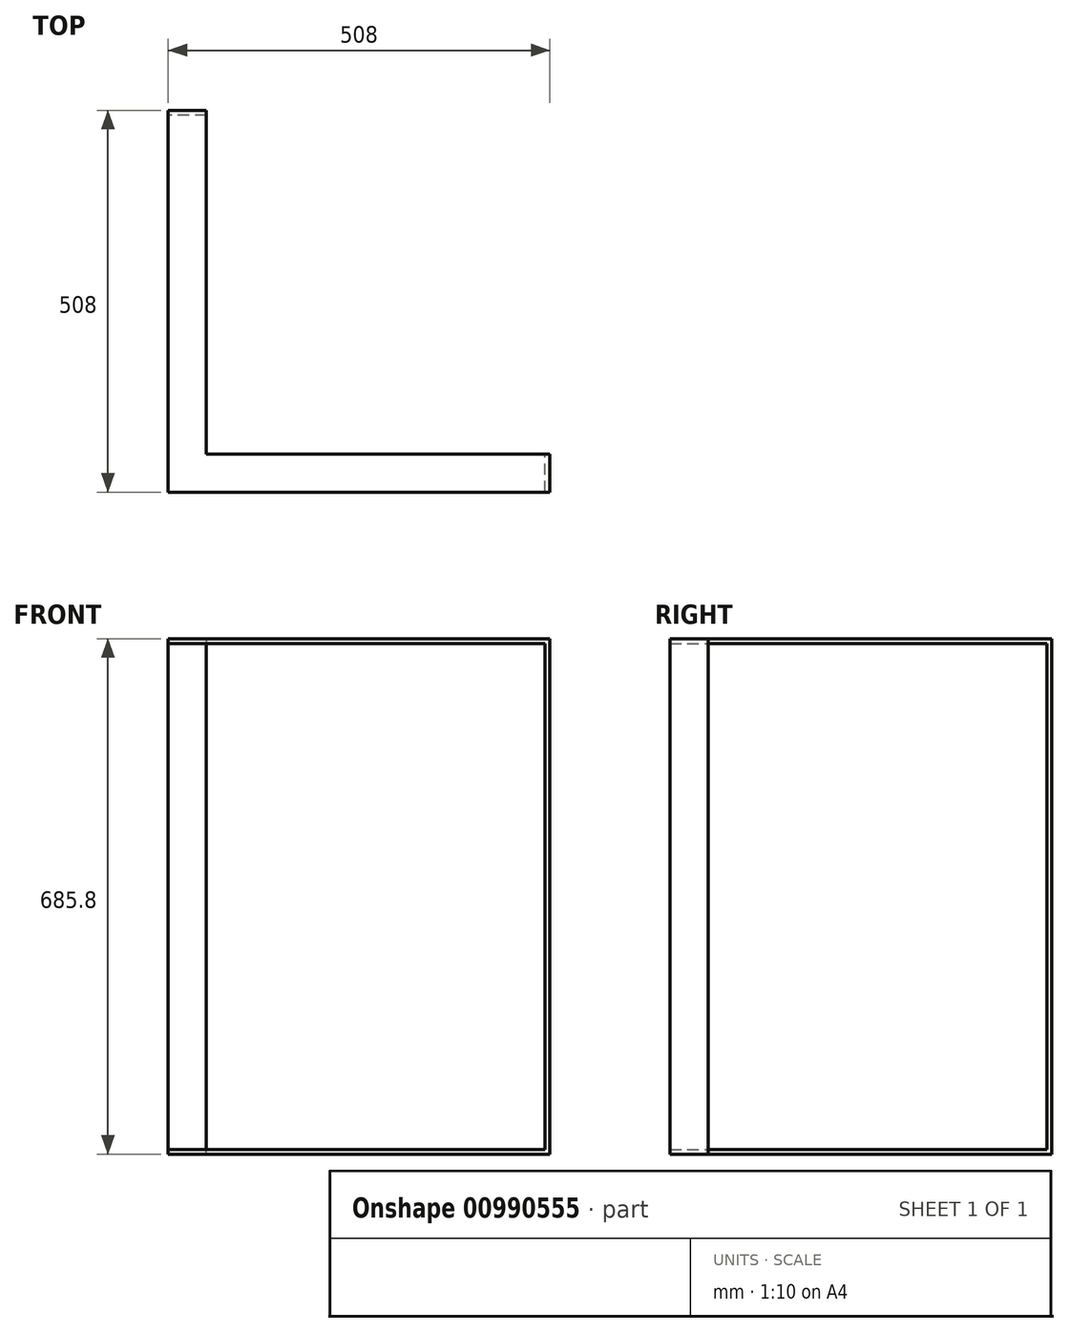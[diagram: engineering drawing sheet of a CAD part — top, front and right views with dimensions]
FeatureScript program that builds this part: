
annotation { "Feature Type Name" : "Feature", "Feature Type Description" : "" }
export const myFeature = defineFeature(function(context is Context, id is Id, definition is map)
    precondition{}
    {
        {
            var Q0;
            Q0=qCreatedBy(makeId("Top.planeOp"),FACE);
            var sketch = newSketch(context, id + "F0", { "sketchPlane" : qUnion([Q0])});
            skLineSegment(sketch, "E0", {"start": v(0, 0) * mm, "end": v(0, 457.2) * mm});
            skLineSegment(sketch, "E1", {"start": v(0, 457.2) * mm, "end": v(-50.8, 457.2) * mm});
            skLineSegment(sketch, "E2", {"start": v(-50.8, 457.2) * mm, "end": v(-50.8, -50.8) * mm});
            skLineSegment(sketch, "E3", {"start": v(-50.8, -50.8) * mm, "end": v(457.2, -50.8) * mm});
            skLineSegment(sketch, "E4", {"start": v(457.2, -50.8) * mm, "end": v(457.2, 0) * mm});
            skLineSegment(sketch, "E5", {"start": v(457.2, 0) * mm, "end": v(0, 0) * mm});
            skSolve(sketch);
        }
        {
            var Q0;
            Q0 = qSketchRegion(id + "F0", true);
            extrude(context, id + "F1", {"entities" : qUnion([Q0]), "depth" : 6.35 * mm, "offsetDistance" : 25.4 * mm});
        }
        {
            var Q0;
            Q0=makeQuery(id+"F1.opExtrude","CAP_FACE",FACE,{"disambiguationData":[OSD([sQuery(id+"F0.wireOp",EDGE,"E0"),sQuery(id+"F0.wireOp",EDGE,"E1"),sQuery(id+"F0.wireOp",EDGE,"E2"),sQuery(id+"F0.wireOp",EDGE,"E3"),sQuery(id+"F0.wireOp",EDGE,"E4"),sQuery(id+"F0.wireOp",EDGE,"E5")])],"isStart":true});
            var sketch = newSketch(context, id + "F2", { "sketchPlane" : qUnion([Q0])});
            skLineSegment(sketch, "E6.bottom", {"start": v(457.2, 50.8) * mm, "end": v(450.85, 50.8) * mm});
            skLineSegment(sketch, "E6.top", {"start": v(457.2, 0) * mm, "end": v(450.85, 0) * mm});
            skLineSegment(sketch, "E6.left", {"start": v(457.2, 50.8) * mm, "end": v(457.2, 0) * mm});
            skLineSegment(sketch, "E6.right", {"start": v(450.85, 50.8) * mm, "end": v(450.85, 0) * mm});
            skSolve(sketch);
        }
        {
            var Q0;
            Q0 = qSketchRegion(id + "F2", true);
            extrude(context, id + "F3", {"entities" : qUnion([Q0]), "operationType" : NewBodyOperationType.ADD, "depth" : 673.1 * mm, "offsetDistance" : 25.4 * mm});
        }
        {
            var Q0;
            Q0=makeQuery(id+"F3.opExtrude","CAP_FACE",FACE,{"disambiguationData":[OSD([sQuery(id+"F2.wireOp",EDGE,"E6.bottom"),sQuery(id+"F2.wireOp",EDGE,"E6.top"),sQuery(id+"F2.wireOp",EDGE,"E6.left"),sQuery(id+"F2.wireOp",EDGE,"E6.right")])],"isStart":false});
            var sketch = newSketch(context, id + "F4", { "sketchPlane" : qUnion([Q0])});
            skLineSegment(sketch, "E7", {"start": v(457.2, 50.8) * mm, "end": v(-50.8, 50.8) * mm});
            skLineSegment(sketch, "E8", {"start": v(-50.8, 50.8) * mm, "end": v(-50.8, -457.2) * mm});
            skLineSegment(sketch, "E9", {"start": v(-50.8, -457.2) * mm, "end": v(0, -457.2) * mm});
            skLineSegment(sketch, "E10", {"start": v(0, -457.2) * mm, "end": v(0, 0) * mm});
            skLineSegment(sketch, "E11", {"start": v(0, 0) * mm, "end": v(457.2, 0) * mm});
            skLineSegment(sketch, "E12", {"start": v(457.2, 0) * mm, "end": v(457.2, 50.8) * mm});
            skSolve(sketch);
        }
        {
            var Q0;
            Q0 = qSketchRegion(id + "F4", true);
            extrude(context, id + "F5", {"entities" : qUnion([Q0]), "operationType" : NewBodyOperationType.ADD, "depth" : 6.35 * mm, "offsetDistance" : 25.4 * mm});
        }
        {
            var Q0;
            Q0=makeQuery(id+"F1.opExtrude","CAP_FACE",FACE,{"disambiguationData":[OSD([sQuery(id+"F0.wireOp",EDGE,"E0"),sQuery(id+"F0.wireOp",EDGE,"E1"),sQuery(id+"F0.wireOp",EDGE,"E2"),sQuery(id+"F0.wireOp",EDGE,"E3"),sQuery(id+"F0.wireOp",EDGE,"E4"),sQuery(id+"F0.wireOp",EDGE,"E5")])],"isStart":true});
            var sketch = newSketch(context, id + "F6", { "sketchPlane" : qUnion([Q0])});
            skLineSegment(sketch, "E13.bottom", {"start": v(0, -457.2) * mm, "end": v(-50.8, -457.2) * mm});
            skLineSegment(sketch, "E13.top", {"start": v(0, -450.85) * mm, "end": v(-50.8, -450.85) * mm});
            skLineSegment(sketch, "E13.left", {"start": v(0, -457.2) * mm, "end": v(0, -450.85) * mm});
            skLineSegment(sketch, "E13.right", {"start": v(-50.8, -457.2) * mm, "end": v(-50.8, -450.85) * mm});
            skSolve(sketch);
        }
        {
            var Q0;
            Q0 = qSketchRegion(id + "F6", true);
            extrude(context, id + "F7", {"entities" : qUnion([Q0]), "operationType" : NewBodyOperationType.ADD, "endBound" : BoundingType.UP_TO_NEXT, "depth" : 25.4 * mm, "offsetDistance" : 25.4 * mm});
        }
    });
